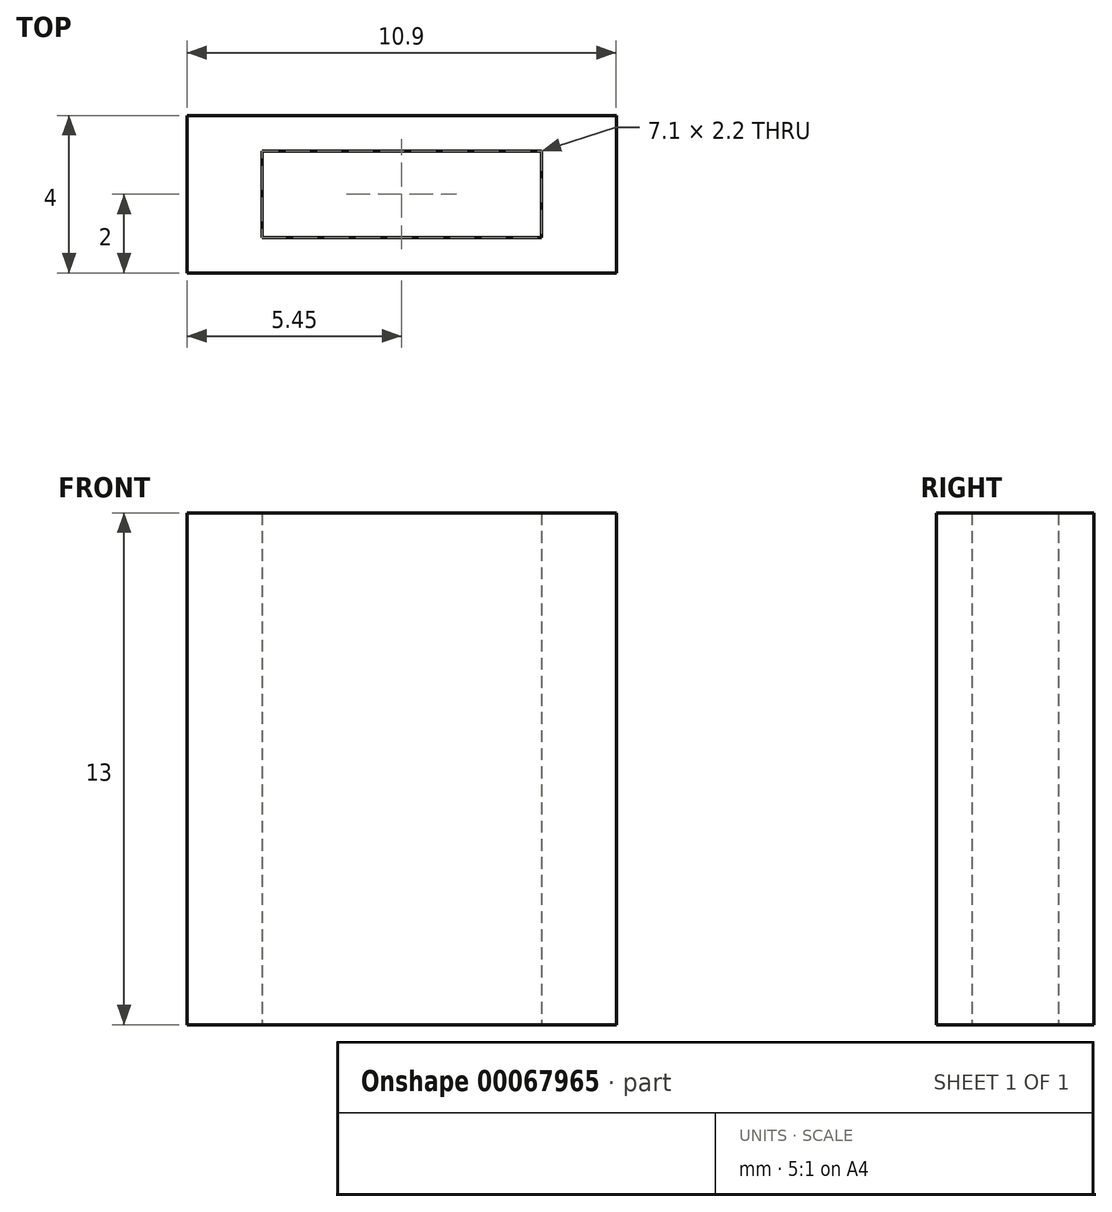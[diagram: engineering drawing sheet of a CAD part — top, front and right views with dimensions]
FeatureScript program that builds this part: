
annotation { "Feature Type Name" : "Feature", "Feature Type Description" : "" }
export const myFeature = defineFeature(function(context is Context, id is Id, definition is map)
    precondition{}
    {
        {
            var Q0;
            Q0=qCreatedBy(makeId("Top.planeOp"),FACE);
            var sketch = newSketch(context, id + "F0", { "sketchPlane" : qUnion([Q0])});
            skLineSegment(sketch, "E0.rect.bottom", {"start": v(5.45, -2) * mm, "end": v(-5.45, -2) * mm});
            skLineSegment(sketch, "E0.rect.top", {"start": v(5.45, 2) * mm, "end": v(-5.45, 2) * mm});
            skLineSegment(sketch, "E0.rect.left", {"start": v(5.45, -2) * mm, "end": v(5.45, 2) * mm});
            skLineSegment(sketch, "E0.rect.right", {"start": v(-5.45, -2) * mm, "end": v(-5.45, 2) * mm});
            skPoint(sketch, "E0.rect.middle", {"position": v(0, 0) * mm});
            skLineSegment(sketch, "E1.rect.bottom", {"start": v(3.55, -1.1) * mm, "end": v(-3.55, -1.1) * mm});
            skLineSegment(sketch, "E1.rect.top", {"start": v(3.55, 1.1) * mm, "end": v(-3.55, 1.1) * mm});
            skLineSegment(sketch, "E1.rect.left", {"start": v(3.55, -1.1) * mm, "end": v(3.55, 1.1) * mm});
            skLineSegment(sketch, "E1.rect.right", {"start": v(-3.55, -1.1) * mm, "end": v(-3.55, 1.1) * mm});
            skSolve(sketch);
        }
        {
            var Q0;
            Q0=makeQuery(id+"F0.imprint","IMPRINT",FACE,{"disambiguationData":[TD([[makeQuery(id+"F0.imprint","IMPRINT",EDGE,{"derivedFrom":sQuery(id+"F0.wireOp",EDGE,"E0.rect.bottom")}),-1.0]])]});
            extrude(context, id + "F1", {"entities" : qUnion([Q0]), "depth" : 13 * mm});
        }
    });
